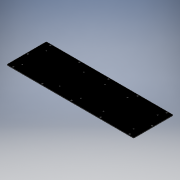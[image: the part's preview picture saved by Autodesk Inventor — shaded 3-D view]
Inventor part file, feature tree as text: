
AUTODESK INVENTOR PART (.ipt)
format: ipt  version: 2018 (Build 220112000, 112)  size: 209,920 bytes
history: native  units: in
note: dims shown in document units (in); Inventor stores cm internally (conversion verified against a paired STEP export)
features: sketch x4, extrude x3, chamfer x1, fillet x1
ambient origin geometry x8: Origin, YZ Plane, XZ Plane, XY Plane, X Axis, Y Axis, Z Axis, Center Point
bodies: Body1 (feature_tree)
feature tree (9):
  sketch  "Sketch4"  dims[d22=17.45in d23=5.45in]
  extrude  "Extrusion3"  Depth=5.45in
  extrude  "Extrusion4"  Depth=0.062in
  extrude  "Extrusion5"  Depth=0.062in
  chamfer  "Chamfer4"  Distance=0.062in
  fillet  "Fillet1"  Radius=17.075in
  sketch  "Sketch5"  dims[d24=0.062in d25=0.0in d26=0.138in]
  sketch  "Sketch6"  dims[d27=0.062in d28=0.0in d29=1.9685in d31=4.0in d32=0.7874in d34=5.075in d37=0.062in d38=0.0in]
  sketch  "Sketch7"  dims[d42=0.025in d43=0.125in d44=45.0deg d45=17.075in d46=0.125in]
